# Revit family: IS_Connect_E7114_BIM_DE
name_source: partatom
category: Plumbing Fixtures
revit_build: Autodesk Revit MEP 2016 (Build: 20161004_0715(x64)
units: mm (PartAtom-declared; Revit-internal decimal feet)

## family parameters
Cut with Voids When Loaded = No
Host = Face
OmniClass Number = 23.45.05.14.14.14
OmniClass Title = Clinic Sinks
Part Type = Normal
Room Calculation Point = No
Round Connector Dimension = Use Diameter
Shared = Yes

## types (1)
- E711401 - Connect semi handrinse pedestal
    Accessoires = www.idealspec.fr
    Assembly Code = C1030200
    CWFU = 0
    Caractéristiques = Cache-Siphon
    Conformité = NF
    ConseilsDInstallation = 0
    Cost = 0 $
    CoûtDeRemplacement = 0
    DateDeCréation = 43351
    Default Elevation = 850 mm  [stored 2.78871 ft]
    Description = Cache-Siphon
    Dimensions = 340 x 175 x 243 mm
    Espace = Interne
    Forme = Complexe
    HWFU = 0
    Hauteur = 340 mm  [stored 1.11549 ft]
    IfcExportAs = IfcSanitaryType
    IfcExportType = WASHHANDBASIN
    InformationsProduit = www.idealspec.fr
    Largeur = 175 mm  [stored 0.574147 ft]
    Longueur = 243 mm
    Marque = Ideal Standard
    Model = E711401
    NBSDescription = Pedestal wash basins
    NBSReference = 45-35-70/365
    PoidsNet = 5,5 Kg
    Profondeur = 0 mm  [stored 0 ft]
    Raccordement = Plomberie
    URL = www.idealspec.fr
    Uniclass2015Code = Pr_40_20_96_63
    Uniclass2015Title = Pedestal wash basins
    UnitéDeMesure = Millimètres
    UnitéDeTemps = An
    UnitéMonétaire = Euro
    UrlDuFabricant = www.idealspec.fr
    WFU = 0

note: [stored X ft] marks values corroborated as IEEE doubles in the binary element streams (Revit-internal decimal feet)

## geometry (parser evidence)
native form markers: Blend x4, Sweep x1
no freeform markers — native parametric forms only
